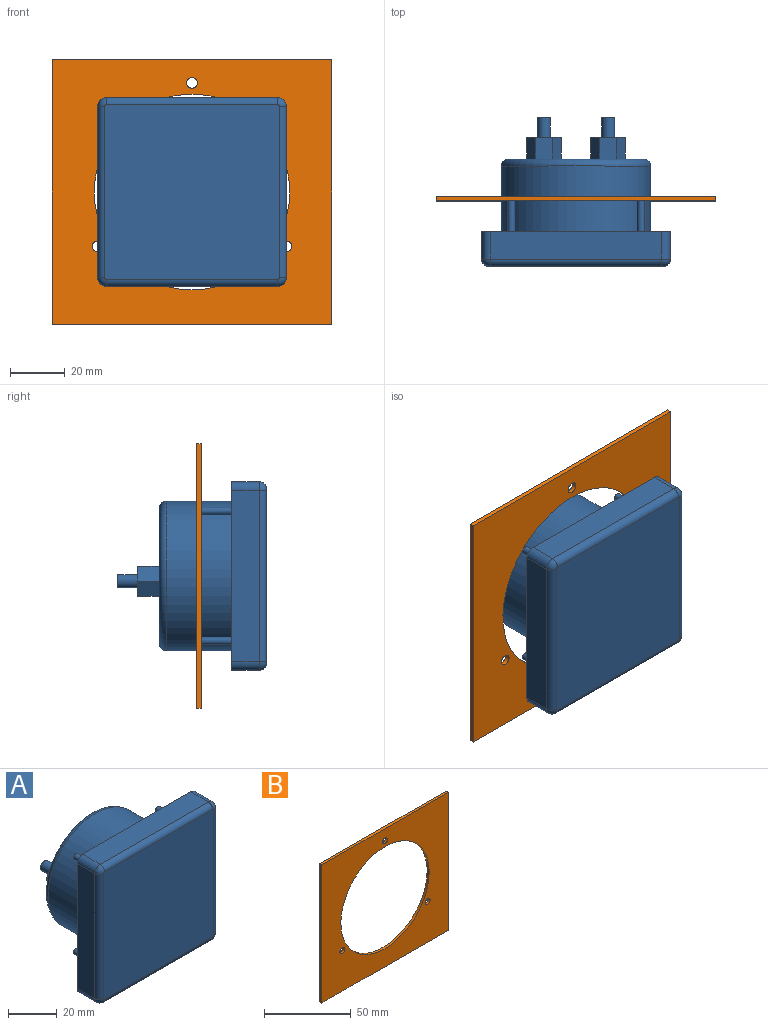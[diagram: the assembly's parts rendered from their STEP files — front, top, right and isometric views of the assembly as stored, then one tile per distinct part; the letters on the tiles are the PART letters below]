
ASSEMBLY  parts=2 mates=1
PART A: 47 faces, bbox 69.2x54.5x69.2 mm
  f0: plane 49.78x49.78mm, normal (0,1,0), area 1737mm2, adj f20,f29,f30,f31,f32,f33,f34,f38
  f1: plane 62.87x10.18mm, normal (0,0,1), area 639.8mm2, adj f2,f8,f10,f16
  f2: cylinder r=3.17mm len=10.18mm, axis (0,1,0), area 50.8mm2, adj f1,f3,f10,f14
  f3: plane 62.87x10.18mm, normal (-1,0,0), area 639.8mm2, adj f2,f4,f10,f12
  f4: cylinder r=3.17mm len=10.18mm, axis (0,1,0), area 50.8mm2, adj f3,f5,f10,f13
  f5: plane 62.87x10.18mm, normal (0,0,-1), area 639.8mm2, adj f4,f6,f10,f15
  f6: cylinder r=3.17mm len=10.18mm, axis (0,1,0), area 50.8mm2, adj f5,f7,f10,f17
  f7: plane 62.87x10.18mm, normal (1,0,0), area 639.8mm2, adj f6,f8,f10,f19
  f8: cylinder r=3.17mm len=10.18mm, axis (0,1,0), area 50.8mm2, adj f1,f7,f10,f18
  f9: plane 64.14x64.14mm, normal (0,-1,0), area 4113mm2, adj f12,f13,f14,f15,f16,f17,f18,f19
  f10: plane 69.22x69.22mm, normal (0,1,0), area 2394.3mm2, adj f1,f2,f3,f4,f5,f6,f7,f8
  f11: cylinder r=27.43mm len=54.86mm, axis (0,-1,0), area 4137.2mm2, adj f10,f20
  f12: cylinder r=2.54mm len=62.87mm, axis (0,0,1), area 250.8mm2, adj f3,f9,f13,f14
  f13: torus R=0.64mm, axis (0,-1,0), area 14.1mm2, adj f4,f9,f12,f15
  f14: torus R=0.64mm, axis (0,-1,0), area 14.1mm2, adj f2,f9,f12,f16
  f15: cylinder r=2.54mm len=62.87mm, axis (-1,0,0), area 250.8mm2, adj f5,f9,f13,f17
  f16: cylinder r=2.54mm len=62.87mm, axis (1,0,0), area 250.8mm2, adj f1,f9,f14,f18
  f17: torus R=0.64mm, axis (0,-1,0), area 14.1mm2, adj f6,f9,f15,f19
  f18: torus R=0.64mm, axis (0,-1,0), area 14.1mm2, adj f8,f9,f16,f19
  f19: cylinder r=2.54mm len=62.87mm, axis (0,0,-1), area 250.8mm2, adj f7,f9,f17,f18
  f20: torus R=24.89mm, axis (0,1,0), area 664.5mm2, adj f0,f11
  f21: cylinder r=1.37mm len=11.61mm, axis (0,-1,0), area 100mm2, adj f10,f22
  f22: plane 2.74x2.74mm, normal (0,1,0), area 5.9mm2, adj f21
  f23: cylinder r=1.37mm len=11.61mm, axis (0,-1,0), area 100mm2, adj f10,f24
  f24: plane 2.74x2.74mm, normal (0,1,0), area 5.9mm2, adj f23
  f25: cylinder r=1.37mm len=11.61mm, axis (0,-1,0), area 100mm2, adj f10,f26
  f26: plane 2.74x2.74mm, normal (0,1,0), area 5.9mm2, adj f25
  f27: cylinder r=1.37mm len=11.61mm, axis (0,-1,0), area 100mm2, adj f10,f28
  f28: plane 2.74x2.74mm, normal (0,1,0), area 5.9mm2, adj f27
  f29: plane 8x6.35mm, normal (0,0,-1), area 50.8mm2, adj f0,f30,f34,f35
  f30: plane 8x5.5mm, normal (-0.87,0,-0.5), area 50.8mm2, adj f0,f29,f31,f35
  f31: plane 8x5.5mm, normal (-0.87,0,0.5), area 50.8mm2, adj f0,f30,f32,f35
  f32: plane 8x6.35mm, normal (0,0,1), area 50.8mm2, adj f0,f31,f33,f35
  f33: plane 8x5.5mm, normal (0.87,0,0.5), area 50.8mm2, adj f0,f32,f34,f35
  f34: plane 8x5.5mm, normal (0.87,0,-0.5), area 50.8mm2, adj f0,f29,f33,f35
  f35: plane 12.7x11mm, normal (0,1,0), area 87mm2, adj f29,f30,f31,f32,f33,f34,f37
  f36: plane 4.75x4.75mm, normal (0,1,0), area 17.7mm2, adj f37
  f37: cylinder r=2.37mm len=7.24mm, axis (0,-1,0), area 108mm2, adj f35,f36
  f38: plane 8x6.35mm, normal (0,0,-1), area 50.8mm2, adj f0,f39,f43,f44
  f39: plane 8x5.5mm, normal (-0.87,0,-0.5), area 50.8mm2, adj f0,f38,f40,f44
  f40: plane 8x5.5mm, normal (-0.87,0,0.5), area 50.8mm2, adj f0,f39,f41,f44
  f41: plane 8x6.35mm, normal (0,0,1), area 50.8mm2, adj f0,f40,f42,f44
  f42: plane 8x5.5mm, normal (0.87,0,0.5), area 50.8mm2, adj f0,f41,f43,f44
  f43: plane 8x5.5mm, normal (0.87,0,-0.5), area 50.8mm2, adj f0,f38,f42,f44
  f44: plane 12.7x11mm, normal (0,1,0), area 87mm2, adj f38,f39,f40,f41,f42,f43,f46
  f45: plane 4.75x4.75mm, normal (0,1,0), area 17.7mm2, adj f46
  f46: cylinder r=2.37mm len=7.24mm, axis (0,-1,0), area 108mm2, adj f44,f45
PART B: 10 faces, bbox 102.5x1.7x97.2 mm
  f0: plane 102.5x1.65mm, normal (0,0,-1), area 169.2mm2, adj f1,f7,f8,f9
  f1: plane 97.16x1.65mm, normal (1,0,0), area 160.4mm2, adj f0,f2,f8,f9
  f2: plane 102.5x1.65mm, normal (0,0,1), area 169.2mm2, adj f1,f7,f8,f9
  f3: cylinder r=35.88mm len=71.76mm, axis (0,1,0), area 372.2mm2, adj f8,f9
  f4: cylinder r=1.98mm len=3.96mm, axis (0,1,0), area 20.6mm2, adj f8,f9
  f5: cylinder r=1.98mm len=3.96mm, axis (0,1,0), area 20.6mm2, adj f8,f9
  f6: cylinder r=1.98mm len=3.96mm, axis (0,1,0), area 20.6mm2, adj f8,f9
  f7: plane 97.16x1.65mm, normal (-1,0,0), area 160.4mm2, adj f0,f2,f8,f9
  f8: plane 102.5x97.16mm, normal (0,-1,0), area 5877.3mm2, adj f0,f1,f2,f3,f4,f5,f6,f7
  f9: plane 102.5x97.16mm, normal (0,1,0), area 5877.3mm2, adj f0,f1,f2,f3,f4,f5,f6,f7
PLACE A t=(10.3,-12.83,2.7)mm
PLACE B t=(10.3,0,2.7)mm fixed
MATE slider A.f11 <-> B.f3  axis (0,-1,0) through (10.3,-0.83,2.7)mm
